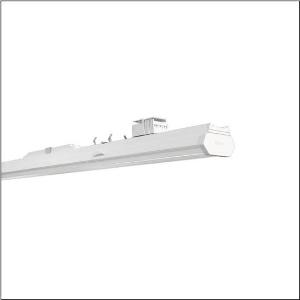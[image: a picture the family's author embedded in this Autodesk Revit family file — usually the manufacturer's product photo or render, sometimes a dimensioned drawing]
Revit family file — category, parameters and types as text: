
# Revit family: licross_r__11_protected_tw_51tp12tnt85x_7ce4
name_source: partatom
category: Lighting Fixtures
units: mm (PartAtom-declared; Revit-internal decimal feet)

## family parameters
Cut with Voids When Loaded = No
Host = Face
Light Source = No
Part Type = Normal
Room Calculation Point = No
Round Connector Dimension = Use Diameter
Shared = No

## types (1)
- --- (1 x LED 2700 K ... 6500 K, 8840 lm, 56 W, 2700K)
    Apparent Load = 56 VA
    CIE Flux Codes = 70 91 97 98 100
    Color Rendering = 80
    Color Temperature = 2700K
    Default Elevation = 1800 mm
    Description = Licross® 11 Protected TW, luminaire insert, of sheet steel, galvanised, coil coated, white, length: 1.500mm, width: 90mm, height: 101mm, LED rated luminous flux: 8.840lm, light colour: 8tw, control gear: DALI DT8, with plug, 5-pole, with phase selection, mains connection: 220..240V, AC, 50/60Hz, rated input power: 56W, halogen-free wiring, primary optical cover: cover, of PMMA, light emission: direct distribution, primary light characteristic: symmetric, protection rating (complete): IP64, insulation class (complete): insulation class I (protective earthing), certification: CE, ENEC, VDE, UKCA, protection symbol: D if used in an environment with conductive dust loads with corresponding accessories, impact resistance: IK06, permissible ambient temperature for indoor applications: -25..+35°C, corresponds to IFS (International Featured Standards) requirements for safety and quality in the food industry, reducing of maximum allowable ambient temperature of 5°C with ceiling mounting, LABS conformity tested according to VDMA 24364:2018-05, packaging unit: 1 piece
    Height = 92 mm
    Lamp = 1 x LED 2700 K ... 6500 K
    Lamp Light Flux = 8840 lm
    Lamp Power = 56 W
    Lamp count = 1
    Length = 1500 mm
    Luminous efficacy = 158 lm/W
    Manufacturer = Siteco
    ModVariant = No
    Model = 51TP12TNT85X
    Mounting Place = Ceiling
    Mounting Type = Pendant
    Number of Poles = 1
    OnlyDefault = Yes
    Power Factor = 1
    Product Name = Licross® 11 Protected TW
    Product group = luminaire insert
    ProductGroupID = 901
    Protection Class = Protection class I
    Protection Degree = IP 64
    RLX_Detail_Level = 1
    RLX_Emergency_Light_Flux = 0 lm
    RLX_Emergency_Type = 0
    RLX_Emergency_Type_DB = No
    RlxData = <blob elided: 20641 chars, md5=0d2ea98a>
    Socket = socket
    Standby Power = 0 W
    System Light Flux = 8840 lm
    System Power = 56 W
    Type Comments = individual setting: CCT=2700K
    Type Image = l_1256148.jpg
    URL = http://relux.com
    VarID = @adj_015819
    Voltage = 0 V
    Weight = 0.00 kg
    Width = 88 mm

## geometry (parser evidence)
native form markers: Blend x4, Sweep x12
no freeform markers — native parametric forms only
